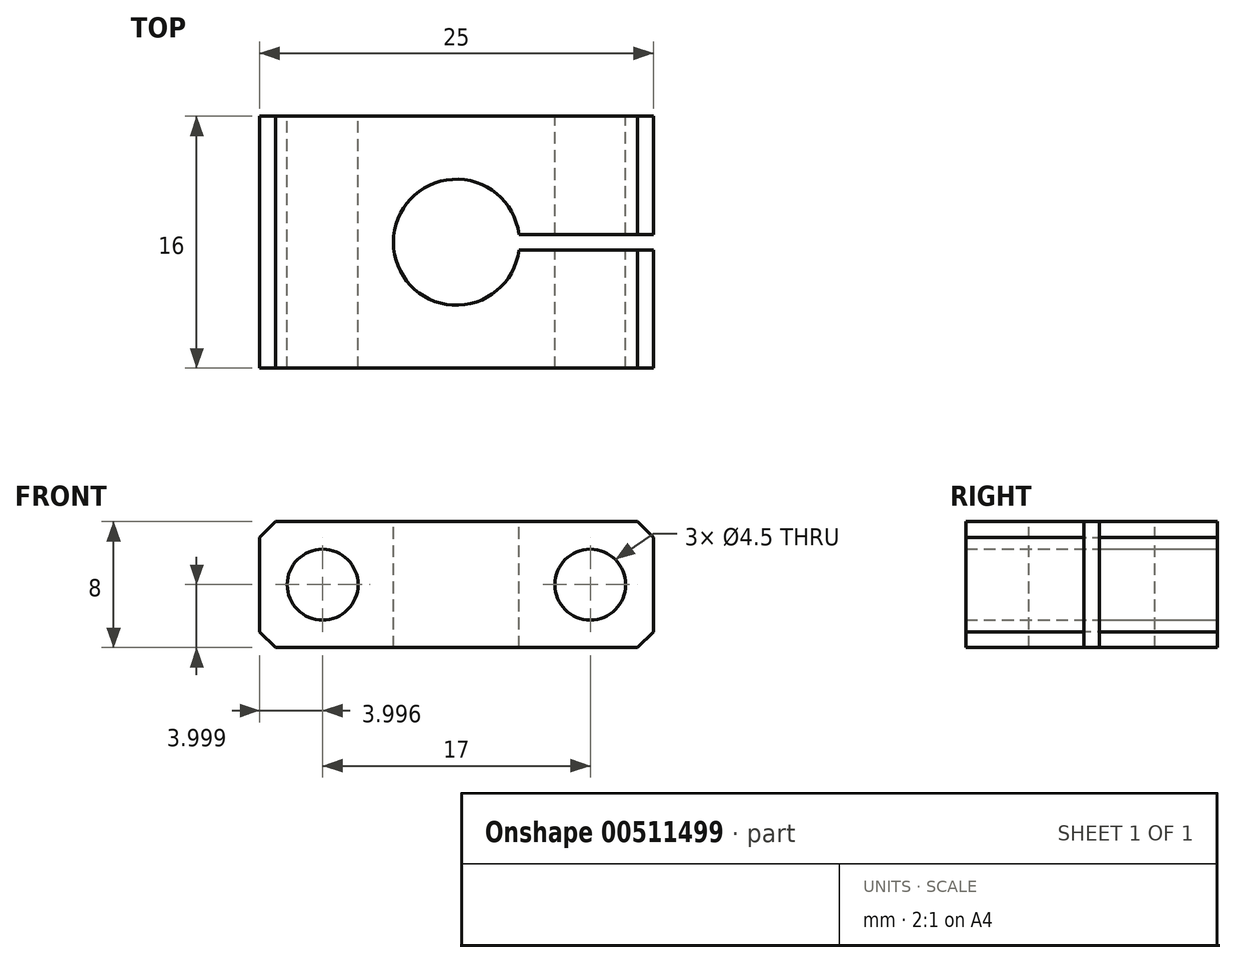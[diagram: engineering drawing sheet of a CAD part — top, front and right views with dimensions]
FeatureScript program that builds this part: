
annotation { "Feature Type Name" : "Feature", "Feature Type Description" : "" }
export const myFeature = defineFeature(function(context is Context, id is Id, definition is map)
    precondition{}
    {
        {
            var Q0;
            Q0=qCreatedBy(makeId("Front.planeOp"),FACE);
            var sketch = newSketch(context, id + "F0", { "sketchPlane" : qUnion([Q0])});
            skLineSegment(sketch, "E0.bottom", {"start": v(-2.28, 7.96) * mm, "end": v(22.72, 7.96) * mm});
            skLineSegment(sketch, "E0.top", {"start": v(-2.28, -0.04) * mm, "end": v(22.72, -0.04) * mm});
            skLineSegment(sketch, "E0.left", {"start": v(-2.28, 7.96) * mm, "end": v(-2.28, -0.04) * mm});
            skLineSegment(sketch, "E0.right", {"start": v(22.72, 7.96) * mm, "end": v(22.72, -0.04) * mm});
            skCircle(sketch, "E1", {"center": v(1.72, 3.96) * mm, "radius": 2.25 * mm});
            skCircle(sketch, "E2", {"center": v(18.72, 3.96) * mm, "radius": 2.25 * mm});
            skSolve(sketch);
        }
        {
            var Q0;
            Q0=makeQuery(id+"F0.imprint","IMPRINT",FACE,{"disambiguationData":[TD([[makeQuery(id+"F0.imprint","IMPRINT",EDGE,{"derivedFrom":sQuery(id+"F0.wireOp",EDGE,"E0.bottom")}),-1.0]])]});
            extrude(context, id + "F1", {"entities" : qUnion([Q0]), "depth" : 16 * mm});
        }
        {
            var Q0;
            Q0=makeQuery(id+"F1.opExtrude","SWEPT_FACE",FACE,{"disambiguationData":[OSD([sQuery(id+"F0.wireOp",EDGE,"E0.bottom")])]});
            var sketch = newSketch(context, id + "F2", { "sketchPlane" : qUnion([Q0])});
            skCircle(sketch, "E3", {"center": v(10.22, -8) * mm, "radius": 4 * mm});
            skPoint(sketch, "E3.centerSnap0", {"position": v(22.72, -8) * mm});
            skPoint(sketch, "E3.centerSnap1", {"position": v(10.22, 0) * mm});
            skSolve(sketch);
        }
        {
            var Q0;
            Q0=makeQuery(id+"F2.imprint","IMPRINT",FACE,{"disambiguationData":[TD([[makeQuery(id+"F2.imprint","IMPRINT",EDGE,{"derivedFrom":sQuery(id+"F2.wireOp",EDGE,"E3")}),1.0]])]});
            extrude(context, id + "F3", {"entities" : qUnion([Q0]), "operationType" : NewBodyOperationType.REMOVE, "oppositeDirection" : true, "depth" : 25 * mm});
        }
        {
            var Q0;
            Q0=makeQuery(id+"F1.opExtrude","SWEPT_EDGE",EDGE,{"disambiguationData":[OSD([sQuery(id+"F0.wireOp",EDGE,"E0.bottom"),sQuery(id+"F0.wireOp",EDGE,"E0.right")])]});
            var Q1;
            Q1=makeQuery(id+"F1.opExtrude","SWEPT_EDGE",EDGE,{"disambiguationData":[OSD([sQuery(id+"F0.wireOp",EDGE,"E0.top"),sQuery(id+"F0.wireOp",EDGE,"E0.right")])]});
            var Q2;
            Q2=makeQuery(id+"F1.opExtrude","SWEPT_EDGE",EDGE,{"disambiguationData":[OSD([sQuery(id+"F0.wireOp",EDGE,"E0.bottom"),sQuery(id+"F0.wireOp",EDGE,"E0.left")])]});
            var Q3;
            Q3=makeQuery(id+"F1.opExtrude","SWEPT_EDGE",EDGE,{"disambiguationData":[OSD([sQuery(id+"F0.wireOp",EDGE,"E0.top"),sQuery(id+"F0.wireOp",EDGE,"E0.left")])]});
            chamfer(context, id + "F4", {"entities" : qUnion([Q0, Q1, Q2, Q3]), "width" : 1 * mm, "tangentPropagation" : true});
        }
        {
            var Q0;
            Q0=makeQuery(id+"F1.opExtrude","SWEPT_FACE",FACE,{"disambiguationData":[OSD([sQuery(id+"F0.wireOp",EDGE,"E0.bottom")])]});
            var sketch = newSketch(context, id + "F5", { "sketchPlane" : qUnion([Q0])});
            skLineSegment(sketch, "E4", {"start": v(14.18, -7.5) * mm, "end": v(22.76, -7.5) * mm});
            skLineSegment(sketch, "E5", {"start": v(22.76, -7.5) * mm, "end": v(22.76, -8.5) * mm});
            skLineSegment(sketch, "E6", {"start": v(22.76, -8.5) * mm, "end": v(14.18, -8.5) * mm});
            skArc(sketch, "E7", {"start": v(14.18, -8.5) * mm, "mid": v(14.22, -8) * mm, "end": v(14.18, -7.5) * mm});
            skSolve(sketch);
        }
        {
            var Q0;
            {var subQ0=sQuery(id+"F5.wireOp",EDGE,"E5");Q0=makeQuery(id+"F5.imprint","IMPRINT",FACE,{"disambiguationData":[TD([[makeQuery(id+"F5.imprint","IMPRINT",EDGE,{"derivedFrom":subQ0}),-1.0]])]});}
            var Q1;
            {var subQ0=sQuery(id+"F5.wireOp",EDGE,"E7");Q1=makeQuery(id+"F5.imprint","IMPRINT",FACE,{"disambiguationData":[TD([[makeQuery(id+"F5.imprint","IMPRINT",EDGE,{"derivedFrom":subQ0}),-1.0]])]});}
            extrude(context, id + "F6", {"entities" : qUnion([Q0, Q1]), "operationType" : NewBodyOperationType.REMOVE, "oppositeDirection" : true, "depth" : 25 * mm});
        }
    });
